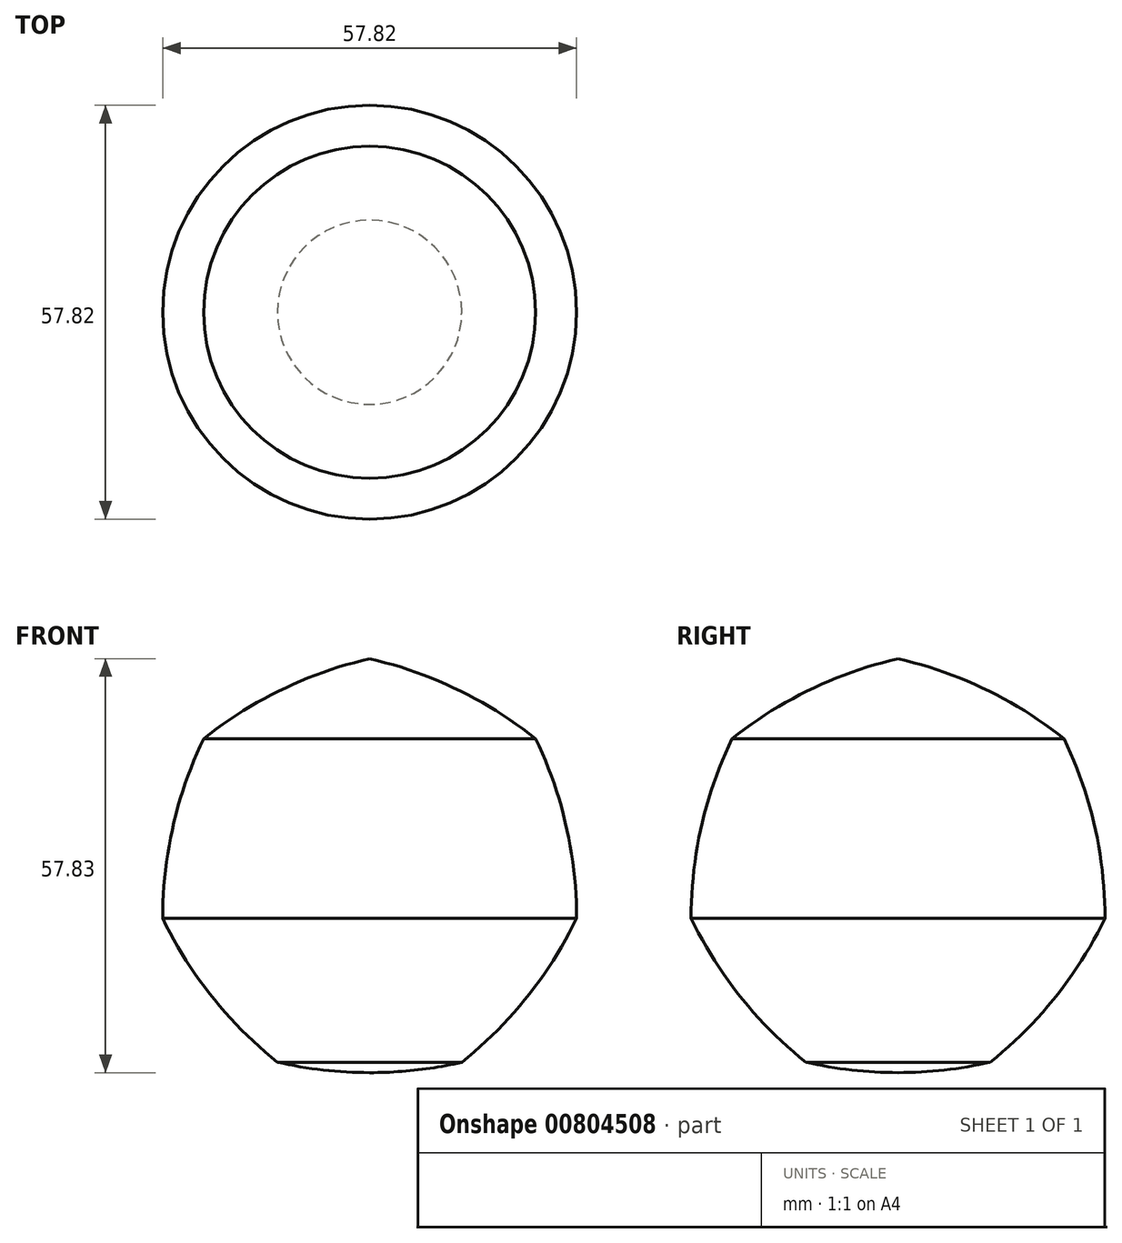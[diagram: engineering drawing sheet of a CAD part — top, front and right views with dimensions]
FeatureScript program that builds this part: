
annotation { "Feature Type Name" : "Feature", "Feature Type Description" : "" }
export const myFeature = defineFeature(function(context is Context, id is Id, definition is map)
    precondition{}
    {
        {
            var Q0;
            Q0=qCreatedBy(makeId("Front.planeOp"),FACE);
            var sketch = newSketch(context, id + "F0", { "sketchPlane" : qUnion([Q0])});
            skCircle(sketch, "E0.cCircle", {"center": v(0, 0) * mm, "radius": 26.72 * mm, "construction": true});
            skLineSegment(sketch, "E0.0", {"start": v(12.87, -26.72) * mm, "end": v(-12.87, -26.72) * mm});
            skLineSegment(sketch, "E0.1", {"start": v(-12.87, -26.72) * mm, "end": v(-28.91, -6.6) * mm});
            skLineSegment(sketch, "E0.2", {"start": v(-28.91, -6.6) * mm, "end": v(-23.19, 18.49) * mm});
            skLineSegment(sketch, "E0.3", {"start": v(-23.19, 18.49) * mm, "end": v(0, 29.66) * mm});
            skLineSegment(sketch, "E0.4", {"start": v(0, 29.66) * mm, "end": v(23.19, 18.49) * mm});
            skLineSegment(sketch, "E0.5", {"start": v(23.19, 18.49) * mm, "end": v(28.91, -6.6) * mm});
            skLineSegment(sketch, "E0.6", {"start": v(28.91, -6.6) * mm, "end": v(12.87, -26.72) * mm});
            skPoint(sketch, "E0.0.midPoint", {"position": v(0, -26.72) * mm});
            skCircle(sketch, "E1", {"center": v(0, 29.66) * mm, "radius": 57.82 * mm});
            skCircle(sketch, "E2", {"center": v(-12.87, -26.72) * mm, "radius": 57.82 * mm});
            skCircle(sketch, "E3", {"center": v(23.19, 18.49) * mm, "radius": 57.82 * mm});
            skCircle(sketch, "E4", {"center": v(-28.91, -6.6) * mm, "radius": 57.82 * mm});
            skCircle(sketch, "E5", {"center": v(28.91, -6.6) * mm, "radius": 57.82 * mm});
            skCircle(sketch, "E6", {"center": v(13, -26.43) * mm, "radius": 57.68 * mm});
            skCircle(sketch, "E7", {"center": v(-23.19, 18.49) * mm, "radius": 57.82 * mm});
            skLineSegment(sketch, "E8", {"start": v(0, 29.66) * mm, "end": v(0, -30.51) * mm});
            skSolve(sketch);
        }
        {
            var Q0;
            {var subQ2=sQuery(id+"F0.wireOp",EDGE,"E0.4");Q0=makeQuery(id+"F0.imprint","IMPRINT",FACE,{"disambiguationData":[TD([[makeQuery(id+"F0.imprint","IMPRINT",EDGE,{"derivedFrom":subQ2}),-1.0]])]});}
            var Q1;
            {var subQ0=sQuery(id+"F0.wireOp",EDGE,"E1");var subQ3=sQuery(id+"F0.wireOp",EDGE,"E8");var subQ5=makeQuery(id+"F0.imprint","INTERSECT",VERTEX,{"derivedFrom":[subQ0,subQ3]});Q1=makeQuery(id+"F0.imprint","IMPRINT",FACE,{"disambiguationData":[TD([[makeQuery(id+"F0.imprint","IMPRINT",EDGE,{"disambiguationData":[TD([[subQ5,1.0]])],"derivedFrom":subQ3}),1.0]])]});}
            var Q2;
            {var subQ0=sQuery(id+"F0.wireOp",EDGE,"E0.6");Q2=makeQuery(id+"F0.imprint","IMPRINT",FACE,{"disambiguationData":[TD([[makeQuery(id+"F0.imprint","IMPRINT",EDGE,{"derivedFrom":subQ0}),1.0]])]});}
            var Q3;
            {var subQ0=sQuery(id+"F0.wireOp",EDGE,"E0.5");Q3=makeQuery(id+"F0.imprint","IMPRINT",FACE,{"disambiguationData":[TD([[makeQuery(id+"F0.imprint","IMPRINT",EDGE,{"derivedFrom":subQ0}),1.0]])]});}
            var Q4;
            {var subQ0=sQuery(id+"F0.wireOp",EDGE,"E0.4");Q4=makeQuery(id+"F0.imprint","IMPRINT",FACE,{"disambiguationData":[TD([[makeQuery(id+"F0.imprint","IMPRINT",EDGE,{"derivedFrom":subQ0}),1.0]])]});}
            var Q5;
            Q5=sQuery(id+"F0.wireOp",EDGE,"E8");
            revolve(context, id + "F1", {"surfaceOperationType" : NewSurfaceOperationType.NEW, "entities" : qUnion([Q0, Q1, Q2, Q3, Q4]), "axis" : qUnion([Q5]), "revolveType" : RevolveType.FULL});
        }
    });
